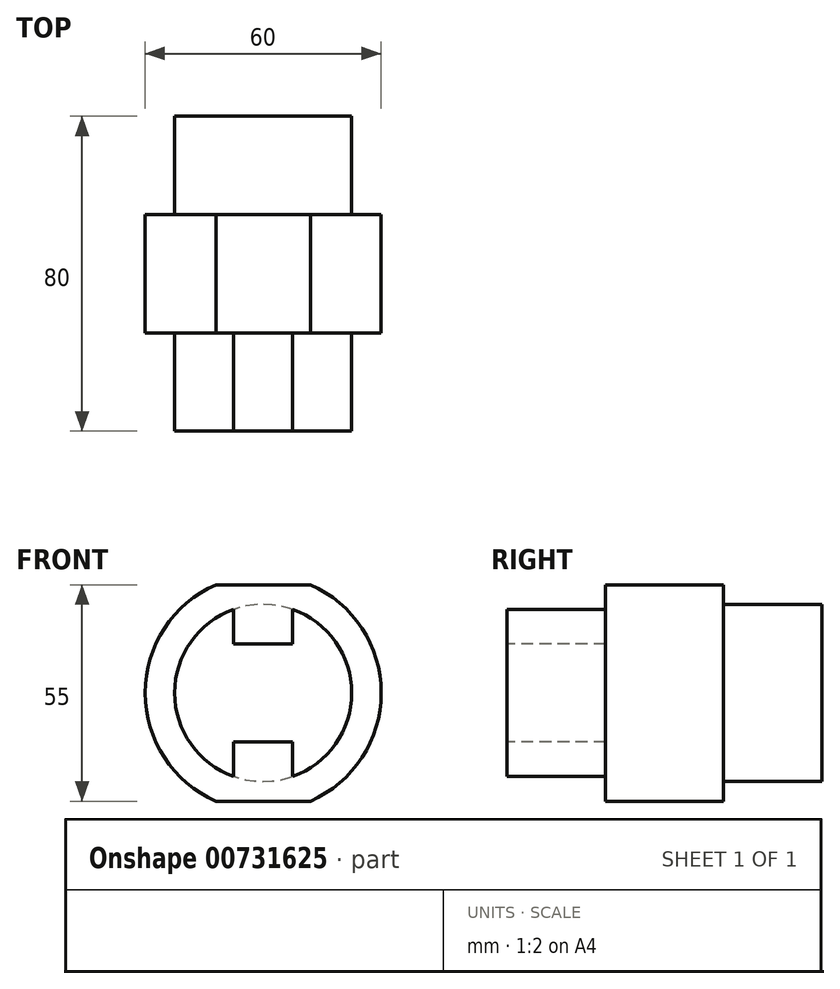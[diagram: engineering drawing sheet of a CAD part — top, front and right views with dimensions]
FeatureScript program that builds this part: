
annotation { "Feature Type Name" : "Feature", "Feature Type Description" : "" }
export const myFeature = defineFeature(function(context is Context, id is Id, definition is map)
    precondition{}
    {
        {
            var Q0;
            Q0=qCreatedBy(makeId("Front.planeOp"),FACE);
            var sketch = newSketch(context, id + "F0", { "sketchPlane" : qUnion([Q0])});
            skCircle(sketch, "E0", {"center": v(0, 0) * mm, "radius": 30 * mm});
            skSolve(sketch);
        }
        {
            var Q0;
            Q0=makeQuery(id+"F0.imprint","IMPRINT",FACE,{"disambiguationData":[TD([[makeQuery(id+"F0.imprint","IMPRINT",EDGE,{"derivedFrom":sQuery(id+"F0.wireOp",EDGE,"E0")}),1.0]])]});
            extrude(context, id + "F1", {"entities" : qUnion([Q0]), "endBound" : BoundingType.SYMMETRIC, "depth" : 30 * mm, "offsetDistance" : 25 * mm});
        }
        {
            var Q0;
            Q0=makeQuery(id+"F1.opExtrude","CAP_FACE",FACE,{"disambiguationData":[OSD([sQuery(id+"F0.wireOp",EDGE,"E0")])],"isStart":false});
            var sketch = newSketch(context, id + "F2", { "sketchPlane" : qUnion([Q0])});
            skCircle(sketch, "E1", {"center": v(0, 0) * mm, "radius": 22.5 * mm});
            skSolve(sketch);
        }
        {
            var Q0;
            Q0 = qSketchRegion(id + "F2", true);
            extrude(context, id + "F3", {"entities" : qUnion([Q0]), "operationType" : NewBodyOperationType.ADD, "depth" : 25 * mm, "offsetDistance" : 25 * mm});
        }
        {
            var Q0;
            Q0=makeQuery(id+"F1.opExtrude","CAP_FACE",FACE,{"disambiguationData":[OSD([sQuery(id+"F0.wireOp",EDGE,"E0")])],"isStart":true});
            var sketch = newSketch(context, id + "F4", { "sketchPlane" : qUnion([Q0])});
            skCircle(sketch, "E2", {"center": v(0, 0) * mm, "radius": 22.5 * mm});
            skSolve(sketch);
        }
        {
            var Q0;
            Q0=makeQuery(id+"F4.imprint","IMPRINT",FACE,{"disambiguationData":[TD([[makeQuery(id+"F4.imprint","IMPRINT",EDGE,{"derivedFrom":sQuery(id+"F4.wireOp",EDGE,"E2")}),1.0]])]});
            extrude(context, id + "F5", {"entities" : qUnion([Q0]), "operationType" : NewBodyOperationType.ADD, "depth" : 25 * mm, "offsetDistance" : 25 * mm});
        }
        {
            var Q0;
            Q0=qCreatedBy(makeId("Front.planeOp"),FACE);
            var sketch = newSketch(context, id + "F6", { "sketchPlane" : qUnion([Q0])});
            skLineSegment(sketch, "E3.bottom", {"start": v(-15, 35.5) * mm, "end": v(15, 35.5) * mm});
            skLineSegment(sketch, "E3.top", {"start": v(-15, 27.5) * mm, "end": v(15, 27.5) * mm});
            skLineSegment(sketch, "E3.left", {"start": v(-15, 35.5) * mm, "end": v(-15, 27.5) * mm});
            skLineSegment(sketch, "E3.right", {"start": v(15, 35.5) * mm, "end": v(15, 27.5) * mm});
            skLineSegment(sketch, "E4.MirrorCS", {"start": v(-15, -27.5) * mm, "end": v(15, -27.5) * mm});
            skLineSegment(sketch, "E5.MirrorCS", {"start": v(-15, -35.5) * mm, "end": v(-15, -27.5) * mm});
            skLineSegment(sketch, "E6.MirrorCS", {"start": v(-15, -35.5) * mm, "end": v(15, -35.5) * mm});
            skLineSegment(sketch, "E7.MirrorCS", {"start": v(15, -35.5) * mm, "end": v(15, -27.5) * mm});
            skSolve(sketch);
        }
        {
            var Q0;
            Q0 = qSketchRegion(id + "F6", true);
            extrude(context, id + "F7", {"entities" : qUnion([Q0]), "operationType" : NewBodyOperationType.REMOVE, "endBound" : BoundingType.SYMMETRIC, "depth" : 30 * mm, "offsetDistance" : 25 * mm});
        }
        {
            var Q0;
            Q0=makeQuery(id+"F3.opExtrude","CAP_FACE",FACE,{"disambiguationData":[OSD([sQuery(id+"F2.wireOp",EDGE,"E1")])],"isStart":false});
            var sketch = newSketch(context, id + "F8", { "sketchPlane" : qUnion([Q0])});
            skLineSegment(sketch, "E8.bottom", {"start": v(-7.5, 24.5) * mm, "end": v(7.5, 24.5) * mm});
            skLineSegment(sketch, "E8.top", {"start": v(-7.5, 12.5) * mm, "end": v(7.5, 12.5) * mm});
            skLineSegment(sketch, "E8.left", {"start": v(-7.5, 24.5) * mm, "end": v(-7.5, 12.5) * mm});
            skLineSegment(sketch, "E8.right", {"start": v(7.5, 24.5) * mm, "end": v(7.5, 12.5) * mm});
            skLineSegment(sketch, "E9.MirrorCS", {"start": v(-7.5, -12.5) * mm, "end": v(7.5, -12.5) * mm});
            skLineSegment(sketch, "E10.MirrorCS", {"start": v(-7.5, -24.5) * mm, "end": v(-7.5, -12.5) * mm});
            skLineSegment(sketch, "E11.MirrorCS", {"start": v(-7.5, -24.5) * mm, "end": v(7.5, -24.5) * mm});
            skLineSegment(sketch, "E12.MirrorCS", {"start": v(7.5, -24.5) * mm, "end": v(7.5, -12.5) * mm});
            skSolve(sketch);
        }
        {
            var Q0;
            Q0 = qSketchRegion(id + "F8", true);
            extrude(context, id + "F9", {"entities" : qUnion([Q0]), "operationType" : NewBodyOperationType.REMOVE, "oppositeDirection" : true, "depth" : 25 * mm, "offsetDistance" : 25 * mm});
        }
    });
